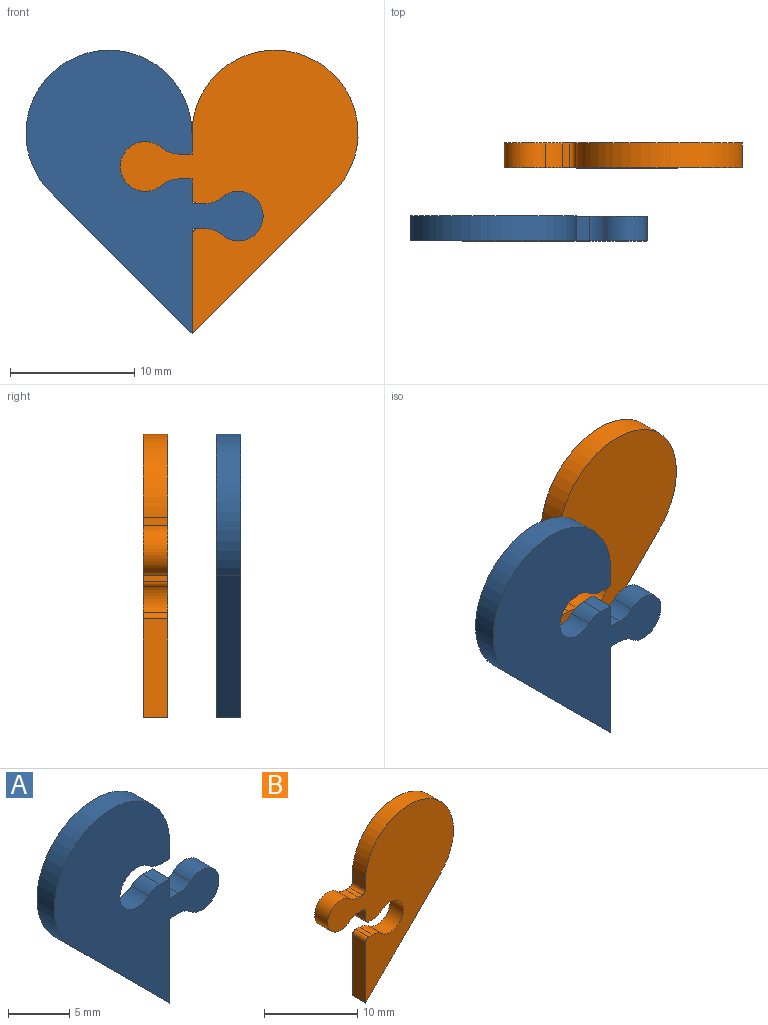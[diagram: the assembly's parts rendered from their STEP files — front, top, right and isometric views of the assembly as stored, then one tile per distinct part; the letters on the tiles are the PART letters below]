
ASSEMBLY  parts=2 mates=1
PART A: 17 faces, bbox 19.1x2x22.8 mm
  f0: plane 2x1.11mm, normal (0,0,-1), area 2.2mm2, adj f1,f14,f15,f16
  f1: plane 2x1.67mm, normal (1,0,0), area 3.3mm2, adj f0,f2,f15,f16
  f2: cylinder r=6.68mm len=13.35mm, axis (0,1,0), area 52.4mm2, adj f1,f3,f15,f16
  f3: plane 11.4x11.4mm, normal (-0.71,0,-0.71), area 32.2mm2, adj f2,f4,f15,f16
  f4: plane 8.45x2mm, normal (1,0,0), area 16.9mm2, adj f3,f5,f15,f16
  f5: plane 2x1.07mm, normal (0,0,-1), area 2.1mm2, adj f4,f6,f15,f16
  f6: cylinder r=2mm len=2mm, axis (0,1,0), area 2.9mm2, adj f5,f7,f15,f16
  f7: cylinder r=2mm len=4mm, axis (0,1,0), area 18.3mm2, adj f6,f8,f15,f16
  f8: cylinder r=2mm len=2mm, axis (0,1,0), area 2.9mm2, adj f7,f9,f15,f16
  f9: plane 2x1.07mm, normal (0,0,1), area 2.1mm2, adj f8,f10,f15,f16
  f10: plane 2x1.99mm, normal (1,0,0), area 4mm2, adj f9,f11,f15,f16
  f11: plane 2x1.11mm, normal (0,0,1), area 2.2mm2, adj f10,f12,f15,f16
  f12: cylinder r=2mm len=2mm, axis (0,1,0), area 2.9mm2, adj f11,f13,f15,f16
  f13: cylinder r=2mm len=4mm, axis (0,1,0), area 18.3mm2, adj f12,f14,f15,f16
  f14: cylinder r=2mm len=2mm, axis (0,1,0), area 2.9mm2, adj f0,f13,f15,f16
  f15: plane 22.79x19.07mm, normal (0,-1,0), area 195mm2, adj f0,f1,f2,f3,f4,f5,f6,f7
  f16: plane 22.79x19.07mm, normal (0,1,0), area 195mm2, adj f0,f1,f2,f3,f4,f5,f6,f7
PART B: 21 faces, bbox 19.1x2x22.8 mm
  f0: plane 2x1.17mm, normal (-1,0,0), area 2.3mm2, adj f14,f15,f16,f17
  f1: plane 2x0.61mm, normal (0,0,1), area 1.2mm2, adj f2,f15,f16,f17
  f2: cylinder r=2mm len=2mm, axis (0,1,0), area 2.9mm2, adj f1,f3,f15,f16
  f3: cylinder r=2mm len=4mm, axis (0,1,0), area 18.3mm2, adj f2,f4,f15,f16
  f4: cylinder r=2mm len=2mm, axis (0,1,0), area 2.9mm2, adj f3,f5,f15,f16
  f5: plane 2x0.61mm, normal (0,0,-1), area 1.2mm2, adj f4,f15,f16,f18
  f6: plane 2x0.99mm, normal (-1,0,0), area 2mm2, adj f15,f16,f18,f19
  f7: plane 2x0.57mm, normal (0,0,-1), area 1.1mm2, adj f8,f15,f16,f19
  f8: cylinder r=2mm len=2mm, axis (0,1,0), area 2.9mm2, adj f7,f9,f15,f16
  f9: cylinder r=2mm len=4mm, axis (0,1,0), area 18.3mm2, adj f8,f10,f15,f16
  f10: cylinder r=2mm len=2mm, axis (0,1,0), area 2.9mm2, adj f9,f11,f15,f16
  f11: plane 2x0.57mm, normal (0,0,1), area 1.1mm2, adj f10,f15,f16,f20
  f12: plane 7.95x2mm, normal (-1,0,0), area 15.9mm2, adj f13,f15,f16,f20
  f13: plane 11.4x11.4mm, normal (0.71,0,-0.71), area 32.2mm2, adj f12,f14,f15,f16
  f14: cylinder r=6.68mm len=13.35mm, axis (0,1,0), area 52.4mm2, adj f0,f13,f15,f16
  f15: plane 22.79x19.11mm, normal (0,-1,0), area 195.1mm2, adj f0,f1,f2,f3,f4,f5,f6,f7
  f16: plane 22.79x19.11mm, normal (0,1,0), area 195.1mm2, adj f0,f1,f2,f3,f4,f5,f6,f7
  f17: cylinder r=0.5mm len=2mm, axis (0,1,0), area 1.6mm2, adj f0,f1,f15,f16
  f18: cylinder r=0.5mm len=2mm, axis (0,-1,0), area 1.6mm2, adj f5,f6,f15,f16
  f19: cylinder r=0.5mm len=2mm, axis (0,-1,0), area 1.6mm2, adj f6,f7,f15,f16
  f20: cylinder r=0.5mm len=2mm, axis (0,-1,0), area 1.6mm2, adj f11,f12,f15,f16
PLACE A t=(0.01,-5.87,-0.01)mm
PLACE B at identity fixed
MATE slider A.f13 <-> B.f3  axis (0,-1,0) through (-3.75,-7.87,1.98)mm
